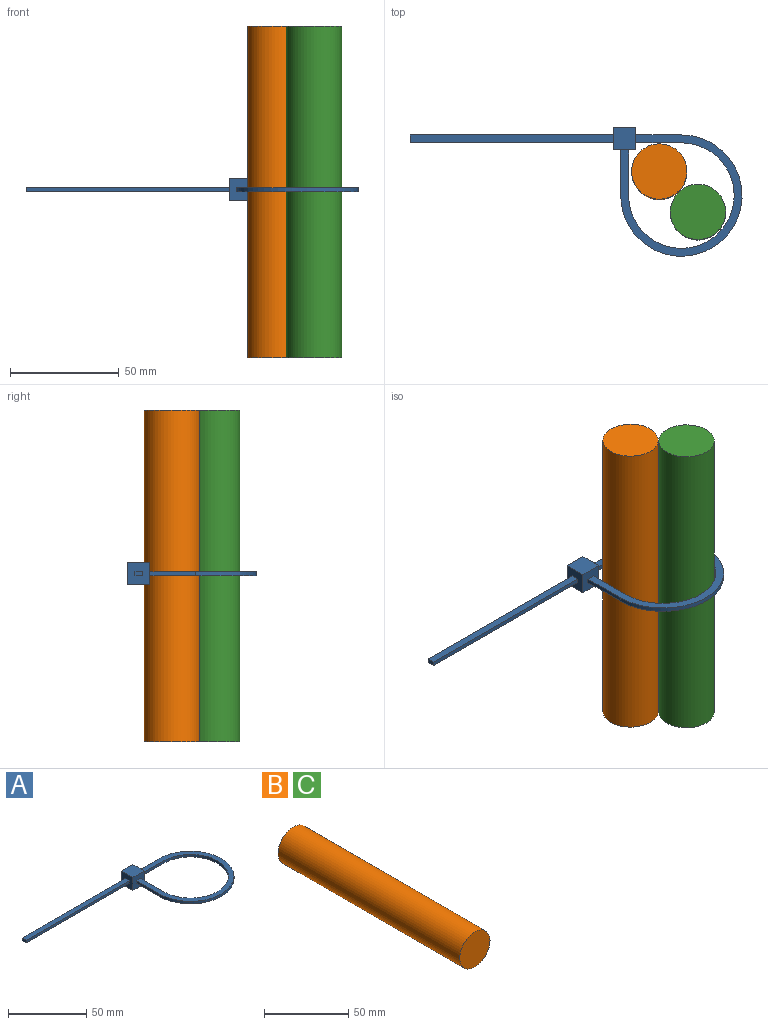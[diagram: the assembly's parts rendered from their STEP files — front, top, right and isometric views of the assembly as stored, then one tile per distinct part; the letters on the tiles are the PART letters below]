
ASSEMBLY  parts=3 mates=2
PART A: 19 faces, bbox 152.5x59x10.2 mm
  f0: plane 10.16x10.16mm, normal (0,1,0), area 103.2mm2, adj f1,f3,f4,f5
  f1: plane 10.16x10.16mm, normal (-1,0,0), area 96.2mm2, adj f0,f2,f4,f5,f14,f15,f16,f17
  f2: plane 10.16x10.16mm, normal (0,-1,0), area 96.2mm2, adj f1,f3,f4,f5,f8,f10,f12,f13
  f3: plane 10.16x10.16mm, normal (1,0,0), area 96.2mm2, adj f0,f2,f4,f5,f8,f9,f10,f11
  f4: plane 10.16x10.16mm, normal (0,0,1), area 103.2mm2, adj f0,f1,f2,f3
  f5: plane 10.16x10.16mm, normal (0,0,-1), area 103.2mm2, adj f0,f1,f2,f3
  f6: cylinder r=24.22mm len=48.44mm, axis (0,0,-1), area 220.5mm2, adj f8,f9,f10,f12
  f7: cylinder r=27.85mm len=55.7mm, axis (0,0,-1), area 253.5mm2, adj f8,f10,f11,f13
  f8: plane 55.7x55.7mm, normal (0,0,-1), area 597.8mm2, adj f2,f3,f6,f7,f9,f11,f12,f13
  f9: plane 20.96x1.93mm, normal (0,-1,0), area 40.5mm2, adj f3,f6,f8,f10
  f10: plane 55.7x55.7mm, normal (0,0,1), area 597.8mm2, adj f2,f3,f6,f7,f9,f11,f12,f13
  f11: plane 20.96x1.93mm, normal (0,1,0), area 40.5mm2, adj f3,f7,f8,f10
  f12: plane 20.96x1.93mm, normal (1,0,0), area 40.5mm2, adj f2,f6,f8,f10
  f13: plane 20.96x1.93mm, normal (-1,0,0), area 40.5mm2, adj f2,f7,f8,f10
  f14: plane 93.52x1.93mm, normal (0,1,0), area 180.7mm2, adj f1,f15,f17,f18
  f15: plane 93.52x3.63mm, normal (0,0,1), area 339.7mm2, adj f1,f14,f16,f18
  f16: plane 93.52x1.93mm, normal (0,-1,0), area 180.7mm2, adj f1,f15,f17,f18
  f17: plane 93.52x3.63mm, normal (0,0,-1), area 339.7mm2, adj f1,f14,f16,f18
  f18: plane 3.63x1.93mm, normal (-1,0,0), area 7mm2, adj f14,f15,f16,f17
PART B: 3 faces, bbox 25.4x152.4x25.4 mm
  f0: cylinder r=12.7mm len=152.4mm, axis (0,-1,0), area 12161mm2, adj f1,f2
  f1: plane 25.4x25.4mm, normal (0,1,0), area 506.7mm2, adj f0
  f2: plane 25.4x25.4mm, normal (0,-1,0), area 506.7mm2, adj f0
PART C: same geometry as B
PLACE A t=(5.08,1.82,0.97)mm
PLACE B rot(axis=(-1,0,0),90deg) t=(20.96,-13.3,76.2)mm
PLACE C rot(axis=(-1,0,0),90deg) t=(38.74,-31.84,76.2)mm
MATE fastened C.f0 <-> A.f8  axis (0,0,1) through (38.74,-31.84,0)mm
MATE fastened B.f0 <-> A.f8  axis (0,0,1) through (20.96,-13.3,0)mm
